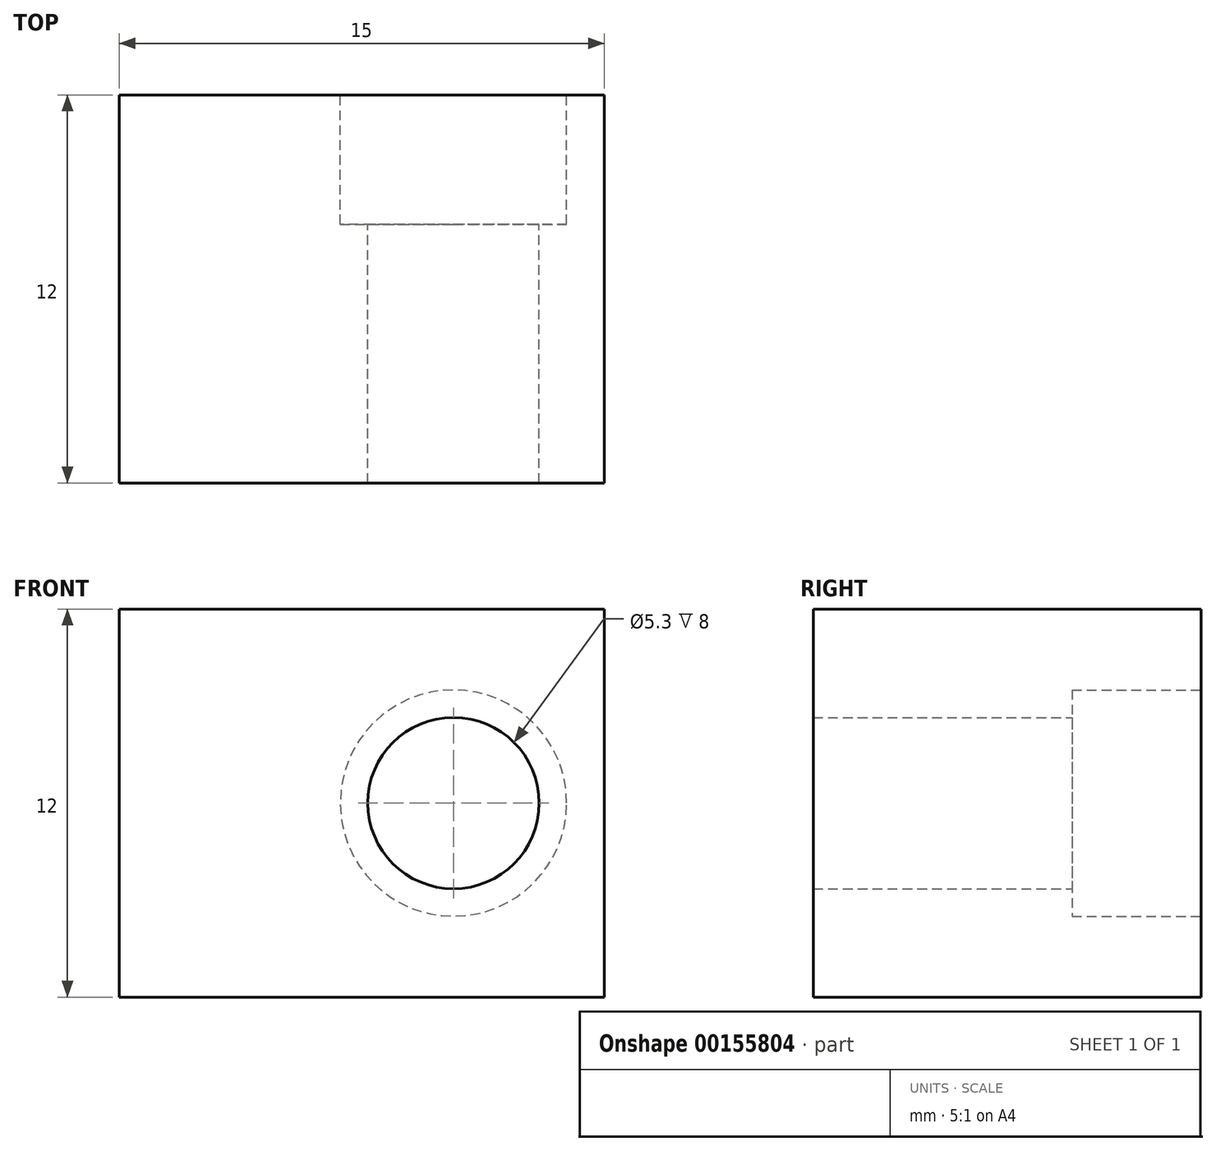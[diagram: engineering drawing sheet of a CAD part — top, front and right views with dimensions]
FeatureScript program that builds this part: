
annotation { "Feature Type Name" : "Feature", "Feature Type Description" : "" }
export const myFeature = defineFeature(function(context is Context, id is Id, definition is map)
    precondition{}
    {
        {
            var Q0;
            Q0=qCreatedBy(makeId("Right.planeOp"),FACE);
            var sketch = newSketch(context, id + "F0", { "sketchPlane" : qUnion([Q0])});
            skLineSegment(sketch, "E0.bottom", {"start": v(6, -6) * mm, "end": v(-6, -6) * mm});
            skLineSegment(sketch, "E0.top", {"start": v(6, 6) * mm, "end": v(-6, 6) * mm});
            skLineSegment(sketch, "E0.left", {"start": v(6, -6) * mm, "end": v(6, 6) * mm});
            skLineSegment(sketch, "E0.right", {"start": v(-6, -6) * mm, "end": v(-6, 6) * mm});
            skPoint(sketch, "E0.middle", {"position": v(0, 0) * mm});
            skSolve(sketch);
        }
        {
            var Q0;
            Q0 = qSketchRegion(id + "F0", true);
            extrude(context, id + "F1", {"entities" : qUnion([Q0]), "depth" : 15 * mm});
        }
        {
            var Q0;
            Q0=makeQuery(id+"F1.opExtrude","SWEPT_FACE",FACE,{"disambiguationData":[OSD([sQuery(id+"F0.wireOp",EDGE,"E0.left")])]});
            var sketch = newSketch(context, id + "F2", { "sketchPlane" : qUnion([Q0])});
            skLineSegment(sketch, "E1", {"start": v(-21.51, 0) * mm, "end": v(6.51, 0) * mm, "construction": true});
            skPoint(sketch, "E1.startSnap0", {"position": v(-15, 0) * mm});
            skCircle(sketch, "E2", {"center": v(-10.34, 0) * mm, "radius": 3.5 * mm});
            skSolve(sketch);
        }
        {
            var Q0;
            Q0 = qSketchRegion(id + "F2", true);
            extrude(context, id + "F3", {"entities" : qUnion([Q0]), "operationType" : NewBodyOperationType.REMOVE, "oppositeDirection" : true, "depth" : 4 * mm});
        }
        {
            var Q0;
            Q0=makeQuery(id+"F3.boolean.opBoolean","COPY",FACE,{"derivedFrom":makeQuery(id+"F3.opExtrude","CAP_FACE",FACE,{"disambiguationData":[OSD([sQuery(id+"F2.wireOp",EDGE,"E2")])],"isStart":false})});
            var sketch = newSketch(context, id + "F4", { "sketchPlane" : qUnion([Q0])});
            skLineSegment(sketch, "E3", {"start": v(-17.42, 0) * mm, "end": v(7.63, 0) * mm, "construction": true});
            skCircle(sketch, "E4", {"center": v(-10.34, 0) * mm, "radius": 2.65 * mm});
            skSolve(sketch);
        }
        {
            var Q0;
            Q0 = qSketchRegion(id + "F4", true);
            extrude(context, id + "F5", {"entities" : qUnion([Q0]), "operationType" : NewBodyOperationType.REMOVE, "oppositeDirection" : true, "depth" : 20 * mm});
        }
    });
